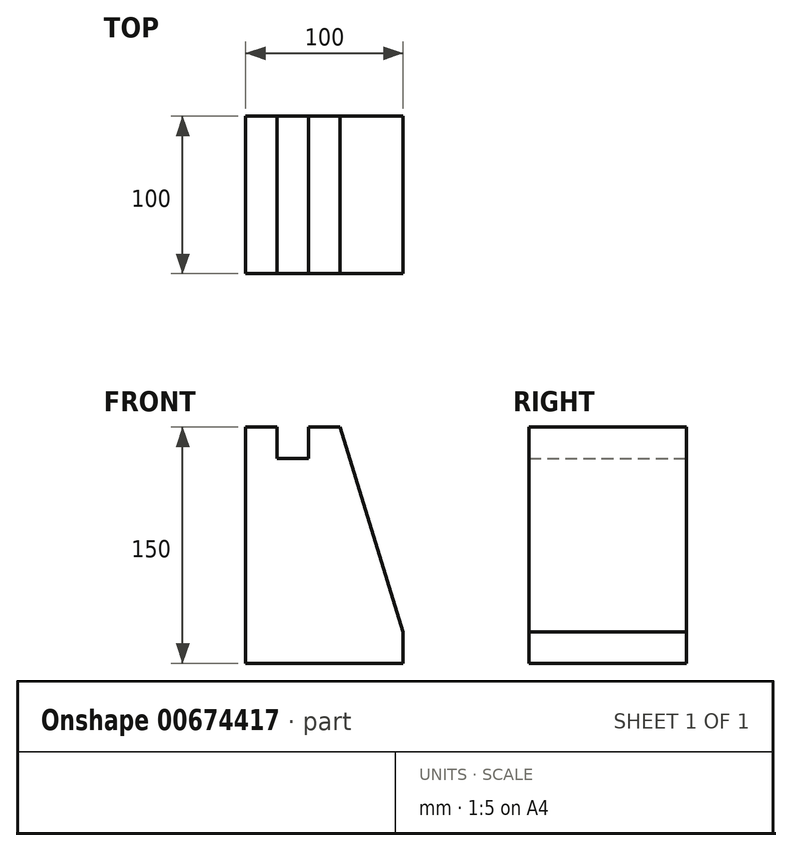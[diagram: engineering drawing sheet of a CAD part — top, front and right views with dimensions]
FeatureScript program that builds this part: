
annotation { "Feature Type Name" : "Feature", "Feature Type Description" : "" }
export const myFeature = defineFeature(function(context is Context, id is Id, definition is map)
    precondition{}
    {
        {
            var Q0;
            Q0=qCreatedBy(makeId("Front.planeOp"),FACE);
            var sketch = newSketch(context, id + "F0", { "sketchPlane" : qUnion([Q0])});
            skLineSegment(sketch, "E0", {"start": v(0, 0) * mm, "end": v(0, 150) * mm});
            skLineSegment(sketch, "E1", {"start": v(0, 150) * mm, "end": v(20, 150) * mm});
            skLineSegment(sketch, "E2", {"start": v(20, 150) * mm, "end": v(20, 130) * mm});
            skLineSegment(sketch, "E3", {"start": v(20, 130) * mm, "end": v(40, 130) * mm});
            skLineSegment(sketch, "E4", {"start": v(40, 130) * mm, "end": v(40, 150) * mm});
            skLineSegment(sketch, "E5", {"start": v(40, 150) * mm, "end": v(60, 150) * mm});
            skLineSegment(sketch, "E6", {"start": v(0, 0) * mm, "end": v(100, 0) * mm});
            skLineSegment(sketch, "E7", {"start": v(100, 0) * mm, "end": v(100, 20) * mm});
            skLineSegment(sketch, "E8", {"start": v(100, 20) * mm, "end": v(60, 150) * mm});
            skSolve(sketch);
        }
        {
            var Q0;
            Q0=makeQuery(id+"F0.imprint","IMPRINT",FACE,{"disambiguationData":[TD([[makeQuery(id+"F0.imprint","IMPRINT",EDGE,{"derivedFrom":sQuery(id+"F0.wireOp",EDGE,"E0")}),-1.0]])]});
            extrude(context, id + "F1", {"entities" : qUnion([Q0]), "depth" : 100 * mm, "offsetDistance" : 25 * mm});
        }
    });
